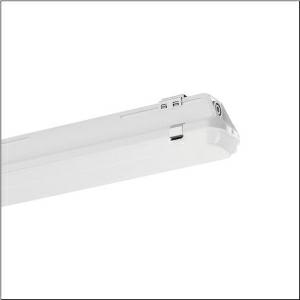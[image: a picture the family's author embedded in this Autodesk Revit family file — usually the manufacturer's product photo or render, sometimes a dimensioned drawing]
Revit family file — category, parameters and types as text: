
# Revit family: monsun_r__11_51fp107p460h_50c3
name_source: partatom
category: Lighting Fixtures
units: mm (PartAtom-declared; Revit-internal decimal feet)

## family parameters
Cut with Voids When Loaded = No
Host = Face
Light Source = No
Part Type = Normal
Room Calculation Point = No
Round Connector Dimension = Use Diameter
Shared = No

## types (1)
- Monsun® 11 (1 x LED, 5800 lm, 32.5 W, 4000K)
    Apparent Load = 33 VA
    CIE Flux Codes = 47 77 93 94 100
    Color Rendering = 80
    Color Temperature = 4000K
    Default Elevation = 1800 mm
    Description = Monsun® 11, damp-proof luminaire, chain hanger, primary optical cover: enclosure, of PMMA, light emission: direct distribution, primary light characteristic: symmetric, installation type: suspended mounting, surface-mounted, horizontal mounting, vertical mounting, LED, rated luminous flux: 5.800lm, luminous efficacy: 178lm/W, light colour: 840, colour temperature: 4000K, control gear: ON/OFF, with terminal, 3-pole, max. 2.5mm², mains connection: 220..240V, AC, 50/60Hz, rated input power: 33W, luminaire housing, of glass-fibre reinforced polyester, uncoated, bright grey, incl. chain hanger, length: 1.590mm, width: 90mm, height: 88mm, clip for enclosure, of stainless steel (V2A), ceiling mounting element, of stainless steel (V2A), chain hanger, of stainless steel (V2A), protection rating (complete): IP66, insulation class (complete): insulation class I (protective earthing), certification: CE, ENEC, VDE, UKCA, protection symbol: D, impact resistance: IK04, permissible operating ambient temperature: -35..+40°C, standard: EN 50419, EN 60598-2-1, no direct snow, no direct sun, no direct rain, for indoor or canopied outdoor use, corresponds to IFS (International Featured Standards) requirements for safety and quality in the food industry, contact your sales advisor before using the luminaires in applications with unclear chemical exposure, large temperature fluctuations or condensation-forming humidity, LABS conformity tested according to VDMA 24364:2018-05, packaging unit: 1 piece
    Height = 89 mm
    Lamp = 1 x LED
    Lamp Light Flux = 5800 lm
    Lamp Power = 32.5 W
    Lamp count = 1
    Length = 1590 mm
    Luminous efficacy = 178 lm/W
    Manufacturer = Siteco
    ModVariant = No
    Model = 51FP107P460H
    Mounting Place = Ceiling
    Mounting Type = Surface mounted
    Number of Poles = 1
    OnlyDefault = Yes
    Power Factor = 1
    Product Name = Monsun® 11
    Product group = damp-proof luminaire
    ProductGroupID = 300
    Protection Class = Protection class I
    Protection Degree = IP 66
    RLX_Detail_Level = 1
    RLX_Emergency_Light_Flux = 0 lm
    RLX_Emergency_Type = 0
    RLX_Emergency_Type_DB = No
    RlxData = <blob elided: 88457 chars, md5=d59efb3d>
    Socket = socket
    Standby Power = 0 W
    System Light Flux = 5800 lm
    System Power = 33 W
    Type Comments = Product without accessories
    Type Image = l_1349237.jpg
    URL = http://relux.com
    VarID = ---
    Voltage = 0 V
    Weight = 0.00 kg
    Width = 90 mm

## geometry (parser evidence)
native form markers: Blend x4, Sweep x12
no freeform markers — native parametric forms only
